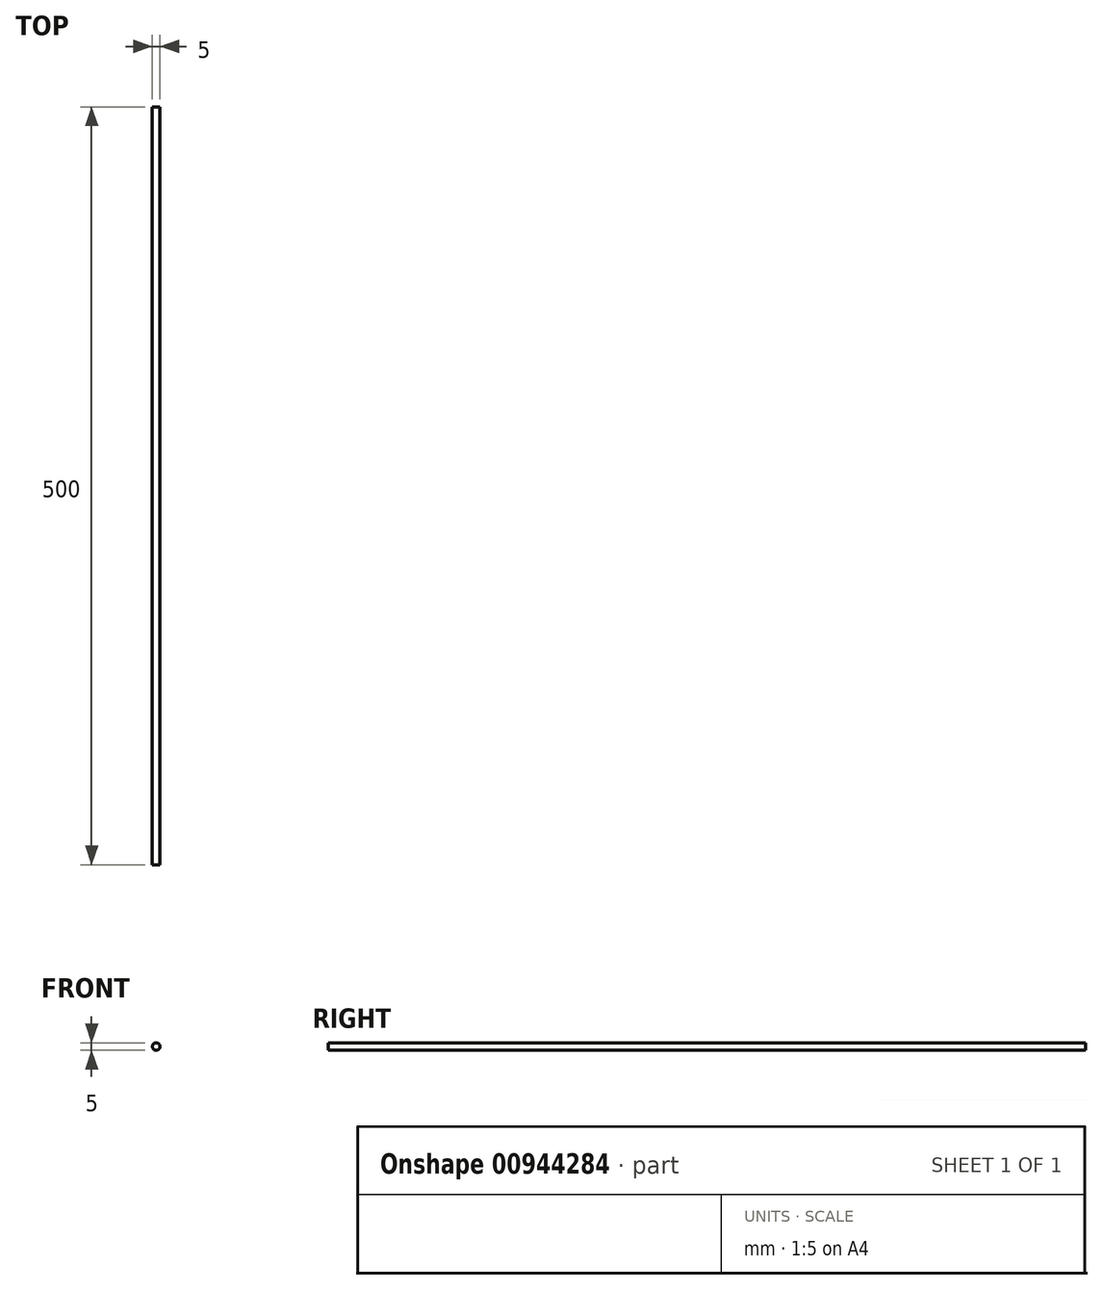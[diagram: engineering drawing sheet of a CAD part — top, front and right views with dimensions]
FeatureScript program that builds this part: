
annotation { "Feature Type Name" : "Feature", "Feature Type Description" : "" }
export const myFeature = defineFeature(function(context is Context, id is Id, definition is map)
    precondition{}
    {
        {
            var Q0;
            Q0=qCreatedBy(makeId("Front.planeOp"),FACE);
            var sketch = newSketch(context, id + "F0", { "sketchPlane" : qUnion([Q0])});
            skCircle(sketch, "E0", {"center": v(0, 0) * mm, "radius": 2.5 * mm});
            skSolve(sketch);
        }
        {
            var Q0;
            Q0=qSketchRegion(id+"F0",true);
            extrude(context, id + "F1", {"entities" : qUnion([Q0]), "depth" : 500 * mm, "offsetDistance" : 25 * mm, "symmetric" : true});
        }
    });
